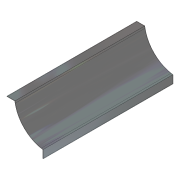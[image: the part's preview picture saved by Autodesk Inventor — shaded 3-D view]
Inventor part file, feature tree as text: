
AUTODESK INVENTOR PART (.ipt)
format: ipt  version: 2012 (Build 160160000, 160)  size: 93,184 bytes
history: native  units: in
note: dims shown in document units (in); Inventor stores cm internally (conversion verified against a paired STEP export)
features: extrude x1, sketch x1
ambient origin geometry x8: Origin, YZ Plane, XZ Plane, XY Plane, X Axis, Y Axis, Z Axis, Center Point
bodies: Solid1 (feature_tree)
feature tree (2):
  extrude  "Extrusion1"  Depth=0.0625in
  sketch  "Sketch1"  dims[d0=0.0625in d1=0.0625in d2=4.0in d3=1.0in d4=16.0in d5=0.0in d6=0.5in]
